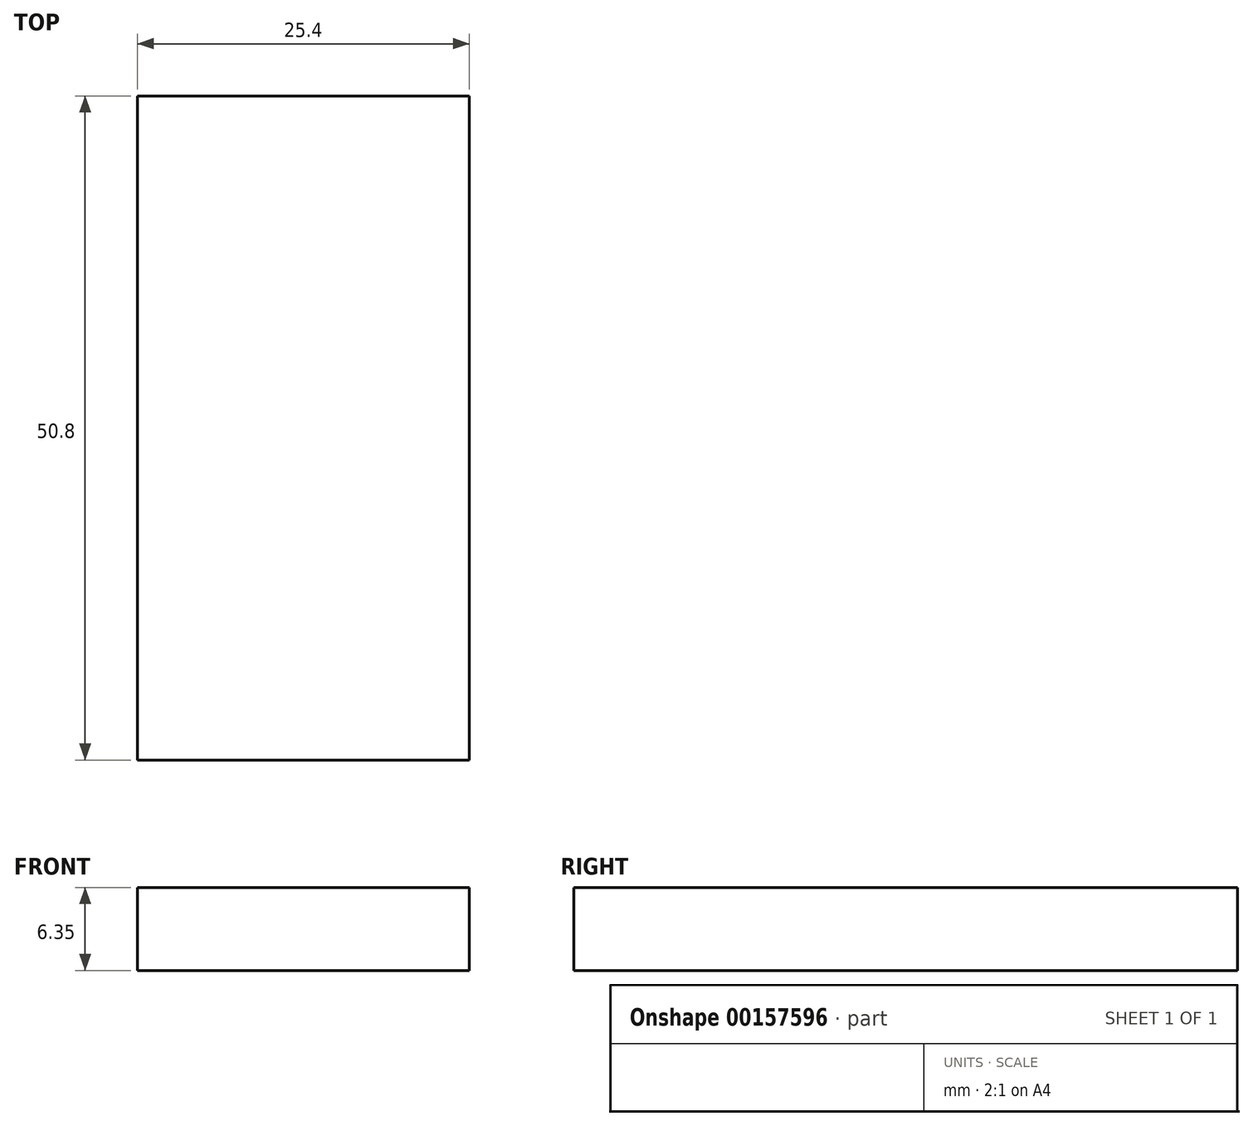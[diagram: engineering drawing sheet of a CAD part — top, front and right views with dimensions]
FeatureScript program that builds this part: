
annotation { "Feature Type Name" : "Feature", "Feature Type Description" : "" }
export const myFeature = defineFeature(function(context is Context, id is Id, definition is map)
    precondition{}
    {
        {
            var Q0;
            Q0=qCreatedBy(makeId("Top.planeOp"),FACE);
            var sketch = newSketch(context, id + "F0", { "sketchPlane" : qUnion([Q0])});
            skLineSegment(sketch, "E0.bottom", {"start": v(12.7, -25.4) * mm, "end": v(-12.7, -25.4) * mm});
            skLineSegment(sketch, "E0.top", {"start": v(12.7, 25.4) * mm, "end": v(-12.7, 25.4) * mm});
            skLineSegment(sketch, "E0.left", {"start": v(12.7, -25.4) * mm, "end": v(12.7, 25.4) * mm});
            skLineSegment(sketch, "E0.right", {"start": v(-12.7, -25.4) * mm, "end": v(-12.7, 25.4) * mm});
            skPoint(sketch, "E0.middle", {"position": v(0, 0) * mm});
            skSolve(sketch);
        }
        {
            var Q0;
            Q0=makeQuery(id+"F0.imprint","IMPRINT",FACE,{"disambiguationData":[TD([[makeQuery(id+"F0.imprint","IMPRINT",EDGE,{"derivedFrom":sQuery(id+"F0.wireOp",EDGE,"E0.bottom")}),-1.0]])]});
            extrude(context, id + "F1", {"entities" : qUnion([Q0]), "depth" : 6.35 * mm});
        }
    });
